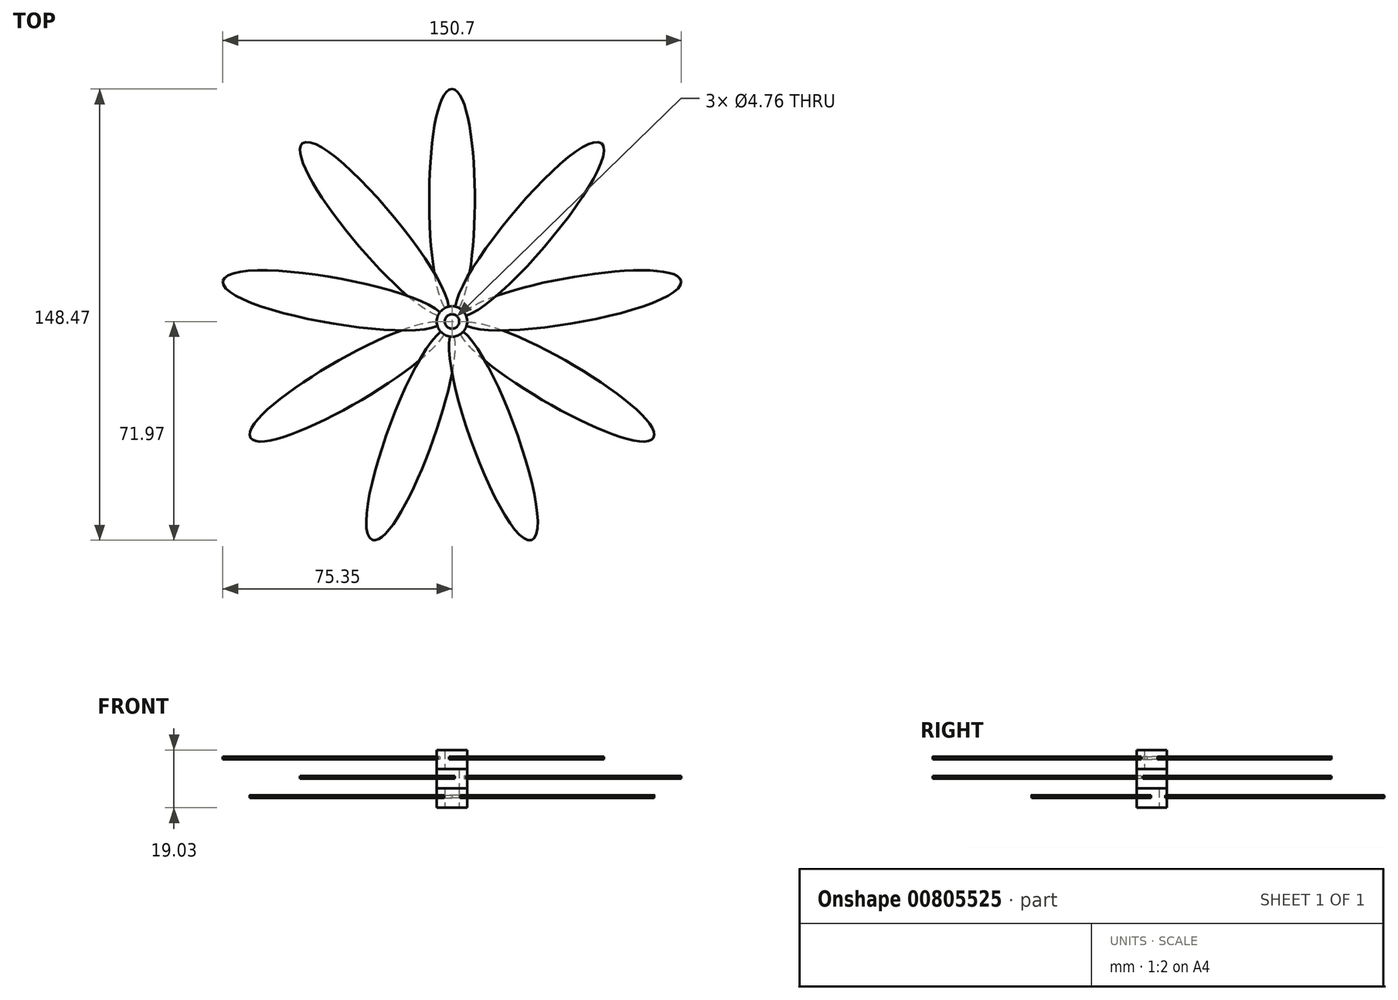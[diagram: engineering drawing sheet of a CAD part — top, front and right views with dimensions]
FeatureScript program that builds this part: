
annotation { "Feature Type Name" : "Feature", "Feature Type Description" : "" }
export const myFeature = defineFeature(function(context is Context, id is Id, definition is map)
    precondition{}
    {
        {
            var Q0;
            Q0=qCreatedBy(makeId("Top.planeOp"),FACE);
            var sketch = newSketch(context, id + "F0", { "sketchPlane" : qUnion([Q0])});
            skCircle(sketch, "E0", {"center": v(0, 0) * mm, "radius": 2.38 * mm});
            skCircle(sketch, "E1", {"center": v(0, 0) * mm, "radius": 5 * mm});
            skCircle(sketch, "E2", {"center": v(0, 0) * mm, "radius": 76.5 * mm, "construction": true});
            skLineSegment(sketch, "E3", {"start": v(0, 0) * mm, "end": v(0, 76.5) * mm, "construction": true});
            skLineSegment(sketch, "E4", {"start": v(0, 0) * mm, "end": v(-66.25, -38.25) * mm, "construction": true});
            skLineSegment(sketch, "E5", {"start": v(0, 0) * mm, "end": v(66.25, -38.25) * mm, "construction": true});
            skFitSpline(sketch, "E6", {"points": [v(-2.06, -1.2) * mm, v(-66.25, -38.25) * mm], "startDerivative": vector(-21.8, 22.05) * mm, "endDerivative": vector(13.32, -27.03) * mm});
            skFitSpline(sketch, "E7", {"points": [v(2.06, -1.2) * mm, v(66.25, -38.25) * mm], "startDerivative": vector(21.8, 22.05) * mm, "endDerivative": vector(-13.32, -27.03) * mm});
            skFitSpline(sketch, "E8", {"points": [v(0, 2.38) * mm, v(0, 76.5) * mm], "startDerivative": vector(-30, 7.86) * mm, "endDerivative": vector(30, 1.97) * mm});
            skFitSpline(sketch, "E9", {"points": [v(-2.06, -1.2) * mm, v(-66.25, -38.25) * mm], "startDerivative": vector(8.2, -29.9) * mm, "endDerivative": vector(-16.67, 24.94) * mm});
            skFitSpline(sketch, "E10", {"points": [v(2.06, -1.2) * mm, v(66.25, -38.25) * mm], "startDerivative": vector(-8.2, -29.9) * mm, "endDerivative": vector(16.67, 24.94) * mm});
            skFitSpline(sketch, "E11", {"points": [v(0, 2.38) * mm, v(0, 76.5) * mm], "startDerivative": vector(30, 7.86) * mm, "endDerivative": vector(-30, 1.97) * mm});
            skLineSegment(sketch, "E12", {"start": v(0, 5) * mm, "end": v(-10, 5) * mm, "construction": true});
            skLineSegment(sketch, "E13", {"start": v(0, 5) * mm, "end": v(10, 5) * mm, "construction": true});
            skLineSegment(sketch, "E14", {"start": v(4.33, -2.5) * mm, "end": v(9.33, 6.16) * mm, "construction": true});
            skLineSegment(sketch, "E15", {"start": v(4.33, -2.5) * mm, "end": v(-0.67, -11.16) * mm, "construction": true});
            skLineSegment(sketch, "E16", {"start": v(-4.33, -2.5) * mm, "end": v(0.67, -11.16) * mm, "construction": true});
            skLineSegment(sketch, "E17", {"start": v(-4.33, -2.5) * mm, "end": v(-9.33, 6.16) * mm, "construction": true});
            skSolve(sketch);
        }
        {
            var Q0;
            {var subQ3=sQuery(id+"F0.wireOp",EDGE,"E8");var subQ5=sQuery(id+"F0.wireOp",EDGE,"E1");var subQ6=makeQuery(id+"F0.imprint","INTERSECT",VERTEX,{"derivedFrom":[subQ5,subQ3]});Q0=makeQuery(id+"F0.imprint","IMPRINT",FACE,{"disambiguationData":[TD([[makeQuery(id+"F0.imprint","IMPRINT",EDGE,{"disambiguationData":[TD([[subQ6,-1.0]])],"derivedFrom":subQ5}),1.0]])]});}
            var Q1;
            {var subQ0=sQuery(id+"F0.wireOp",EDGE,"E6");var subQ1=sQuery(id+"F0.wireOp",EDGE,"E1");var subQ2=makeQuery(id+"F0.imprint","INTERSECT",VERTEX,{"derivedFrom":[subQ1,subQ0]});Q1=makeQuery(id+"F0.imprint","IMPRINT",FACE,{"disambiguationData":[TD([[makeQuery(id+"F0.imprint","IMPRINT",EDGE,{"disambiguationData":[TD([[subQ2,-1.0]])],"derivedFrom":subQ1}),1.0]])]});}
            var Q2;
            {var subQ0=sQuery(id+"F0.wireOp",EDGE,"E9");var subQ5=sQuery(id+"F0.wireOp",EDGE,"E1");var subQ6=makeQuery(id+"F0.imprint","INTERSECT",VERTEX,{"derivedFrom":[subQ5,subQ0]});Q2=makeQuery(id+"F0.imprint","IMPRINT",FACE,{"disambiguationData":[TD([[makeQuery(id+"F0.imprint","IMPRINT",EDGE,{"disambiguationData":[TD([[subQ6,-1.0]])],"derivedFrom":subQ5}),1.0]])]});}
            var Q3;
            {var subQ0=sQuery(id+"F0.wireOp",EDGE,"E10");var subQ1=sQuery(id+"F0.wireOp",EDGE,"E1");var subQ2=makeQuery(id+"F0.imprint","INTERSECT",VERTEX,{"derivedFrom":[subQ1,subQ0]});Q3=makeQuery(id+"F0.imprint","IMPRINT",FACE,{"disambiguationData":[TD([[makeQuery(id+"F0.imprint","IMPRINT",EDGE,{"disambiguationData":[TD([[subQ2,-1.0]])],"derivedFrom":subQ1}),1.0]])]});}
            var Q4;
            {var subQ3=sQuery(id+"F0.wireOp",EDGE,"E11");var subQ5=sQuery(id+"F0.wireOp",EDGE,"E1");var subQ6=makeQuery(id+"F0.imprint","INTERSECT",VERTEX,{"derivedFrom":[subQ5,subQ3]});Q4=makeQuery(id+"F0.imprint","IMPRINT",FACE,{"disambiguationData":[TD([[makeQuery(id+"F0.imprint","IMPRINT",EDGE,{"disambiguationData":[TD([[subQ6,1.0]])],"derivedFrom":subQ5}),1.0]])]});}
            var Q5;
            {var subQ0=sQuery(id+"F0.wireOp",EDGE,"E8");var subQ1=sQuery(id+"F0.wireOp",EDGE,"E1");var subQ2=makeQuery(id+"F0.imprint","INTERSECT",VERTEX,{"derivedFrom":[subQ1,subQ0]});Q5=makeQuery(id+"F0.imprint","IMPRINT",FACE,{"disambiguationData":[TD([[makeQuery(id+"F0.imprint","IMPRINT",EDGE,{"disambiguationData":[TD([[subQ2,1.0]])],"derivedFrom":subQ1}),1.0]])]});}
            extrude(context, id + "F1", {"entities" : qUnion([Q0, Q1, Q2, Q3, Q4, Q5]), "depth" : 6.34 * mm, "offsetDistance" : 25 * mm, "symmetric" : true});
        }
        {
            var Q0;
            {var subQ0=sQuery(id+"F0.wireOp",EDGE,"E6");var subQ1=sQuery(id+"F0.wireOp",EDGE,"E1");var subQ2=makeQuery(id+"F0.imprint","INTERSECT",VERTEX,{"derivedFrom":[subQ1,subQ0]});Q0=makeQuery(id+"F0.imprint","IMPRINT",FACE,{"disambiguationData":[TD([[makeQuery(id+"F0.imprint","IMPRINT",EDGE,{"disambiguationData":[TD([[subQ2,-1.0]])],"derivedFrom":subQ1}),-1.0]])]});}
            var Q1;
            {var subQ0=sQuery(id+"F0.wireOp",EDGE,"E10");var subQ1=sQuery(id+"F0.wireOp",EDGE,"E1");var subQ2=makeQuery(id+"F0.imprint","INTERSECT",VERTEX,{"derivedFrom":[subQ1,subQ0]});Q1=makeQuery(id+"F0.imprint","IMPRINT",FACE,{"disambiguationData":[TD([[makeQuery(id+"F0.imprint","IMPRINT",EDGE,{"disambiguationData":[TD([[subQ2,-1.0]])],"derivedFrom":subQ1}),-1.0]])]});}
            var Q2;
            {var subQ0=sQuery(id+"F0.wireOp",EDGE,"E8");var subQ1=sQuery(id+"F0.wireOp",EDGE,"E1");var subQ2=makeQuery(id+"F0.imprint","INTERSECT",VERTEX,{"derivedFrom":[subQ1,subQ0]});Q2=makeQuery(id+"F0.imprint","IMPRINT",FACE,{"disambiguationData":[TD([[makeQuery(id+"F0.imprint","IMPRINT",EDGE,{"disambiguationData":[TD([[subQ2,1.0]])],"derivedFrom":subQ1}),-1.0]])]});}
            extrude(context, id + "F2", {"entities" : qUnion([Q0, Q1, Q2]), "operationType" : NewBodyOperationType.ADD, "depth" : 1 * mm, "offsetDistance" : 25 * mm});
        }
        {
            var Q0;
            Q0=makeQuery(id+"F1.opExtrude","SWEPT_BODY",BODY,{"disambiguationData":[OSD([sQuery(id+"F0.wireOp",EDGE,"E0"),sQuery(id+"F0.wireOp",EDGE,"E1")])]});
            transform(context, id + "F3", {"entities" : qUnion([Q0]), "transformType" : TransformType.TRANSLATION_3D, "dx" : 0 * mm, "dy" : 0 * mm, "dz" : 6.35 * mm, "makeCopy" : true});
        }
        {
            var Q0;
            Q0=qCreatedBy(makeId("Front.planeOp"),FACE);
            var sketch = newSketch(context, id + "F4", { "sketchPlane" : qUnion([Q0])});
            skLineSegment(sketch, "E18", {"start": v(0, 0) * mm, "end": v(0, 32.82) * mm, "construction": true});
            skSolve(sketch);
        }
        {
            var Q0;
            Q0=makeQuery(id+"F3.opPattern","COPY",BODY,{"derivedFrom":makeQuery(id+"F1.opExtrude","SWEPT_BODY",BODY,{"disambiguationData":[OSD([sQuery(id+"F0.wireOp",EDGE,"E0"),sQuery(id+"F0.wireOp",EDGE,"E1")])]}),"instanceName":"1"});
            var Q1;
            Q1=sQuery(id+"F4.wireOp",EDGE,"E18");
            transform(context, id + "F5", {"entities" : qUnion([Q0]), "transformType" : TransformType.ROTATION, "transformAxis" : qUnion([Q1]), "angle" : 40 * degree, "makeCopy" : false});
        }
        {
            var Q0;
            Q0=makeQuery(id+"F3.opPattern","COPY",BODY,{"derivedFrom":makeQuery(id+"F1.opExtrude","SWEPT_BODY",BODY,{"disambiguationData":[OSD([sQuery(id+"F0.wireOp",EDGE,"E0"),sQuery(id+"F0.wireOp",EDGE,"E1")])]}),"instanceName":"1"});
            transform(context, id + "F6", {"entities" : qUnion([Q0]), "transformType" : TransformType.TRANSLATION_3D, "dx" : 0 * mm, "dy" : 0 * mm, "dz" : 6.34 * mm, "makeCopy" : true});
        }
        {
            var Q0;
            Q0=makeQuery(id+"F6.opPattern","COPY",BODY,{"derivedFrom":makeQuery(id+"F3.opPattern","COPY",BODY,{"derivedFrom":makeQuery(id+"F1.opExtrude","SWEPT_BODY",BODY,{"disambiguationData":[OSD([sQuery(id+"F0.wireOp",EDGE,"E0"),sQuery(id+"F0.wireOp",EDGE,"E1")])]}),"instanceName":"1"}),"instanceName":"1"});
            var Q1;
            Q1=sQuery(id+"F4.wireOp",EDGE,"E18");
            transform(context, id + "F7", {"entities" : qUnion([Q0]), "transformType" : TransformType.ROTATION, "transformAxis" : qUnion([Q1]), "angle" : 40 * degree, "makeCopy" : false});
        }
    });
